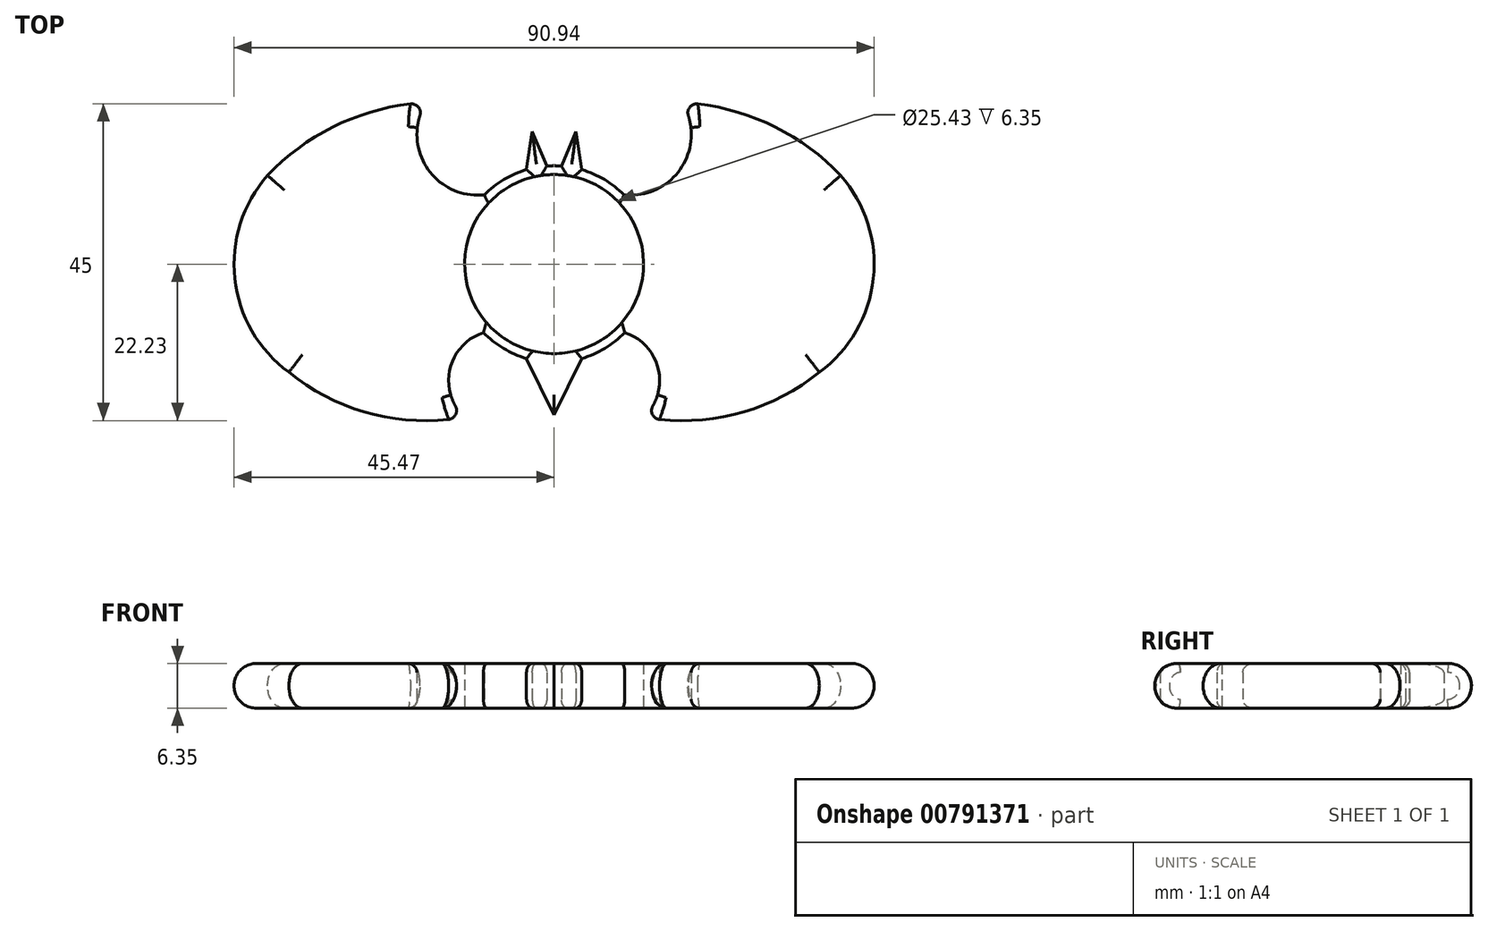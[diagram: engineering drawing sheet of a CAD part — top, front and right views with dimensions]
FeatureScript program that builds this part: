
annotation { "Feature Type Name" : "Feature", "Feature Type Description" : "" }
export const myFeature = defineFeature(function(context is Context, id is Id, definition is map)
    precondition{}
    {
        {
            var Q0;
            Q0=qCreatedBy(makeId("Top.planeOp"),FACE);
            var sketch = newSketch(context, id + "F0", { "sketchPlane" : qUnion([Q0])});
            skCircle(sketch, "E0", {"center": v(0, 0) * mm, "radius": 13.97 * mm});
            skArc(sketch, "E1", {"start": v(37.68, -15.37) * mm, "mid": v(45.36, -2.05) * mm, "end": v(40.7, 12.6) * mm});
            skArc(sketch, "E2", {"start": v(-18.2, 22.95) * mm, "mid": v(-30.45, 19.93) * mm, "end": v(-40.7, 12.6) * mm});
            skArc(sketch, "E3", {"start": v(-18.2, 22.95) * mm, "mid": v(-18.15, 13.81) * mm, "end": v(-9.93, 9.83) * mm});
            skArc(sketch, "E4.trimOffspring", {"start": v(-40.7, 12.6) * mm, "mid": v(-45.36, -2.05) * mm, "end": v(-37.68, -15.37) * mm});
            skArc(sketch, "E5.MirrorCS", {"start": v(18.2, 22.95) * mm, "mid": v(18.15, 13.81) * mm, "end": v(9.93, 9.83) * mm});
            skArc(sketch, "E6.MirrorCS", {"start": v(18.2, 22.95) * mm, "mid": v(30.45, 19.93) * mm, "end": v(40.7, 12.6) * mm});
            skArc(sketch, "E7", {"start": v(-37.68, -15.37) * mm, "mid": v(-25.91, -21.27) * mm, "end": v(-12.76, -21.74) * mm});
            skArc(sketch, "E8", {"start": v(-10.03, -9.72) * mm, "mid": v(-14.81, -14.95) * mm, "end": v(-12.76, -21.74) * mm});
            skArc(sketch, "E9.MirrorCS", {"start": v(10.03, -9.72) * mm, "mid": v(14.81, -14.95) * mm, "end": v(12.76, -21.74) * mm});
            skArc(sketch, "E10.MirrorCS", {"start": v(37.68, -15.37) * mm, "mid": v(25.91, -21.27) * mm, "end": v(12.76, -21.74) * mm});
            skPoint(sketch, "E11.end.orphan", {"position": v(2.34, 18.82) * mm});
            skPoint(sketch, "E12.orphan", {"position": v(3.92, 13.4) * mm});
            skPoint(sketch, "E13.end.orphan", {"position": v(-1.04, 13.93) * mm});
            skPoint(sketch, "E14.end.orphan", {"position": v(-2.23, 18.82) * mm});
            skPoint(sketch, "E15.MirrorCS.end.orphan", {"position": v(1.04, 13.93) * mm});
            skPoint(sketch, "E15.MirrorCS.start.orphan", {"position": v(2.23, 18.82) * mm});
            skPoint(sketch, "E16.end.orphan", {"position": v(-4.8, 18.35) * mm});
            skPoint(sketch, "E17.MirrorCS.end.orphan", {"position": v(4.8, 18.35) * mm});
            skLineSegment(sketch, "E18", {"start": v(-1.04, 13.93) * mm, "end": v(-3.1, 18.83) * mm});
            skLineSegment(sketch, "E19", {"start": v(-3.1, 18.83) * mm, "end": v(-3.92, 13.4) * mm});
            skLineSegment(sketch, "E20.MirrorCS", {"start": v(1.04, 13.93) * mm, "end": v(3.1, 18.83) * mm});
            skLineSegment(sketch, "E21.MirrorCS", {"start": v(3.1, 18.83) * mm, "end": v(3.92, 13.4) * mm});
            skPoint(sketch, "E22.end.orphan", {"position": v(0, -21.45) * mm});
            skPoint(sketch, "E22.start.orphan", {"position": v(-4.01, -13.38) * mm});
            skPoint(sketch, "E23.MirrorCS.start.orphan", {"position": v(4.01, -13.38) * mm});
            skPoint(sketch, "E24.MirrorCS.end.orphan", {"position": v(-3.92, -13.4) * mm});
            skPoint(sketch, "E24.MirrorCS.start.orphan", {"position": v(-3.1, -18.83) * mm});
            skLineSegment(sketch, "E25", {"start": v(-3.92, -13.4) * mm, "end": v(0, -21.45) * mm});
            skLineSegment(sketch, "E26.MirrorCS", {"start": v(3.92, -13.4) * mm, "end": v(0, -21.45) * mm});
            skLineSegment(sketch, "E27", {"start": v(-26.42, 0) * mm, "end": v(-31.16, 0) * mm});
            skLineSegment(sketch, "E28", {"start": v(26.42, 0) * mm, "end": v(31.16, 0) * mm});
            skCircle(sketch, "E29", {"center": v(0, 0) * mm, "radius": 12.71 * mm});
            skSolve(sketch);
        }
        {
            var Q0;
            Q0=qSketchRegion(id+"F0",true);
            extrude(context, id + "F1", {"entities" : qUnion([Q0]), "depth" : 6.35 * mm, "offsetDistance" : 25.4 * mm});
        }
        {
            var Q0;
            Q0=makeQuery(id+"F1.opExtrude","CAP_EDGE",EDGE,{"disambiguationData":[OSD([sQuery(id+"F0.wireOp",EDGE,"E4.trimOffspring")])],"isStart":false});
            var Q1;
            Q1=makeQuery(id+"F1.opExtrude","CAP_EDGE",EDGE,{"disambiguationData":[OSD([sQuery(id+"F0.wireOp",EDGE,"E1")])],"isStart":false});
            var Q2;
            Q2=makeQuery(id+"F1.opExtrude","CAP_EDGE",EDGE,{"disambiguationData":[OSD([sQuery(id+"F0.wireOp",EDGE,"E1")])],"isStart":true});
            var Q3;
            Q3=makeQuery(id+"F1.opExtrude","CAP_EDGE",EDGE,{"disambiguationData":[OSD([sQuery(id+"F0.wireOp",EDGE,"E4.trimOffspring")])],"isStart":true});
            fillet(context, id + "F2", {"entities" : qUnion([Q0, Q1, Q2, Q3]), "radius" : 3.17 * mm, "tangentPropagation" : true, "allowEdgeOverflow" : false});
        }
        {
            var Q0;
            Q0=makeQuery(id+"F2.opFillet","BLEND_EDGE",EDGE,{"blendedFrom":[makeQuery(id+"F1.opExtrude","CAP_EDGE",EDGE,{"disambiguationData":[OSD([sQuery(id+"F0.wireOp",EDGE,"E4.trimOffspring")])],"isStart":false}),makeQuery(id+"F1.opExtrude","SWEPT_FACE",FACE,{"disambiguationData":[OSD([sQuery(id+"F0.wireOp",EDGE,"E3")])]})],"blendedInto":[makeQuery(id+"F1.opExtrude","SWEPT_FACE",FACE,{"disambiguationData":[OSD([sQuery(id+"F0.wireOp",EDGE,"E3")])]})]});
            var Q1;
            Q1=makeQuery(id+"F2.opFillet","BLEND_EDGE",EDGE,{"blendedFrom":[makeQuery(id+"F1.opExtrude","CAP_EDGE",EDGE,{"disambiguationData":[OSD([sQuery(id+"F0.wireOp",EDGE,"E4.trimOffspring")])],"isStart":true}),makeQuery(id+"F1.opExtrude","SWEPT_FACE",FACE,{"disambiguationData":[OSD([sQuery(id+"F0.wireOp",EDGE,"E3")])]})],"blendedInto":[makeQuery(id+"F1.opExtrude","SWEPT_FACE",FACE,{"disambiguationData":[OSD([sQuery(id+"F0.wireOp",EDGE,"E3")])]})]});
            var Q2;
            Q2=makeQuery(id+"F1.opExtrude","CAP_EDGE",EDGE,{"disambiguationData":[OSD([sQuery(id+"F0.wireOp",EDGE,"E8")])],"isStart":false});
            var Q3;
            Q3=makeQuery(id+"F1.opExtrude","CAP_EDGE",EDGE,{"disambiguationData":[OSD([sQuery(id+"F0.wireOp",EDGE,"E9.MirrorCS")])],"isStart":false});
            var Q4;
            Q4=makeQuery(id+"F1.opExtrude","CAP_EDGE",EDGE,{"disambiguationData":[OSD([sQuery(id+"F0.wireOp",EDGE,"E5.MirrorCS")])],"isStart":false});
            var Q5;
            {var subQ0=sQuery(id+"F0.wireOp",EDGE,"E0");Q5=makeQuery(id+"F1.opExtrude","CAP_EDGE",EDGE,{"disambiguationData":[OSD([subQ0]),TDD([makeQuery(id+"F0.imprint","IMPRINT",EDGE,{"disambiguationData":[TD([[makeQuery(id+"F0.imprint","INTERSECT",VERTEX,{"derivedFrom":[subQ0,sQuery(id+"F0.wireOp",EDGE,"E3")]}),1.0]])],"derivedFrom":subQ0})])],"isStart":false});}
            var Q6;
            Q6=makeQuery(id+"F1.opExtrude","CAP_EDGE",EDGE,{"disambiguationData":[OSD([sQuery(id+"F0.wireOp",EDGE,"E19")])],"isStart":false});
            var Q7;
            {var subQ0=sQuery(id+"F0.wireOp",EDGE,"E0");Q7=makeQuery(id+"F1.opExtrude","CAP_EDGE",EDGE,{"disambiguationData":[OSD([subQ0]),TDD([makeQuery(id+"F0.imprint","IMPRINT",EDGE,{"disambiguationData":[TD([[makeQuery(id+"F0.imprint","INTERSECT",VERTEX,{"derivedFrom":[subQ0,sQuery(id+"F0.wireOp",EDGE,"E18")]}),1.0]])],"derivedFrom":subQ0})])],"isStart":false});}
            var Q8;
            Q8=makeQuery(id+"F1.opExtrude","CAP_EDGE",EDGE,{"disambiguationData":[OSD([sQuery(id+"F0.wireOp",EDGE,"E20.MirrorCS")])],"isStart":false});
            var Q9;
            {var subQ0=sQuery(id+"F0.wireOp",EDGE,"E0");Q9=makeQuery(id+"F1.opExtrude","CAP_EDGE",EDGE,{"disambiguationData":[OSD([subQ0]),TDD([makeQuery(id+"F0.imprint","IMPRINT",EDGE,{"disambiguationData":[TD([[makeQuery(id+"F0.imprint","INTERSECT",VERTEX,{"derivedFrom":[subQ0,sQuery(id+"F0.wireOp",EDGE,"E5.MirrorCS")]}),-1.0]])],"derivedFrom":subQ0})])],"isStart":false});}
            var Q10;
            {var subQ0=sQuery(id+"F0.wireOp",EDGE,"E0");Q10=makeQuery(id+"F1.opExtrude","CAP_EDGE",EDGE,{"disambiguationData":[OSD([subQ0]),TDD([makeQuery(id+"F0.imprint","IMPRINT",EDGE,{"disambiguationData":[TD([[makeQuery(id+"F0.imprint","INTERSECT",VERTEX,{"derivedFrom":[subQ0,sQuery(id+"F0.wireOp",EDGE,"E5.MirrorCS")]}),-1.0]])],"derivedFrom":subQ0})])],"isStart":true});}
            var Q11;
            Q11=makeQuery(id+"F1.opExtrude","CAP_EDGE",EDGE,{"disambiguationData":[OSD([sQuery(id+"F0.wireOp",EDGE,"E21.MirrorCS")])],"isStart":true});
            var Q12;
            {var subQ0=sQuery(id+"F0.wireOp",EDGE,"E0");Q12=makeQuery(id+"F1.opExtrude","CAP_EDGE",EDGE,{"disambiguationData":[OSD([subQ0]),TDD([makeQuery(id+"F0.imprint","IMPRINT",EDGE,{"disambiguationData":[TD([[makeQuery(id+"F0.imprint","INTERSECT",VERTEX,{"derivedFrom":[subQ0,sQuery(id+"F0.wireOp",EDGE,"E18")]}),1.0]])],"derivedFrom":subQ0})])],"isStart":true});}
            var Q13;
            Q13=makeQuery(id+"F1.opExtrude","CAP_EDGE",EDGE,{"disambiguationData":[OSD([sQuery(id+"F0.wireOp",EDGE,"E18")])],"isStart":true});
            var Q14;
            Q14=makeQuery(id+"F1.opExtrude","CAP_EDGE",EDGE,{"disambiguationData":[OSD([sQuery(id+"F0.wireOp",EDGE,"E19")])],"isStart":true});
            var Q15;
            {var subQ0=sQuery(id+"F0.wireOp",EDGE,"E0");Q15=makeQuery(id+"F1.opExtrude","CAP_EDGE",EDGE,{"disambiguationData":[OSD([subQ0]),TDD([makeQuery(id+"F0.imprint","IMPRINT",EDGE,{"disambiguationData":[TD([[makeQuery(id+"F0.imprint","INTERSECT",VERTEX,{"derivedFrom":[subQ0,sQuery(id+"F0.wireOp",EDGE,"E3")]}),1.0]])],"derivedFrom":subQ0})])],"isStart":true});}
            var Q16;
            {var subQ0=sQuery(id+"F0.wireOp",EDGE,"E0");Q16=makeQuery(id+"F1.opExtrude","CAP_EDGE",EDGE,{"disambiguationData":[OSD([subQ0]),TDD([makeQuery(id+"F0.imprint","IMPRINT",EDGE,{"disambiguationData":[TD([[makeQuery(id+"F0.imprint","INTERSECT",VERTEX,{"derivedFrom":[subQ0,sQuery(id+"F0.wireOp",EDGE,"E8")]}),-1.0]])],"derivedFrom":subQ0})])],"isStart":false});}
            var Q17;
            Q17=makeQuery(id+"F1.opExtrude","CAP_EDGE",EDGE,{"disambiguationData":[OSD([sQuery(id+"F0.wireOp",EDGE,"E25")])],"isStart":false});
            var Q18;
            Q18=makeQuery(id+"F1.opExtrude","CAP_EDGE",EDGE,{"disambiguationData":[OSD([sQuery(id+"F0.wireOp",EDGE,"E26.MirrorCS")])],"isStart":false});
            var Q19;
            {var subQ0=sQuery(id+"F0.wireOp",EDGE,"E0");Q19=makeQuery(id+"F1.opExtrude","CAP_EDGE",EDGE,{"disambiguationData":[OSD([subQ0]),TDD([makeQuery(id+"F0.imprint","IMPRINT",EDGE,{"disambiguationData":[TD([[makeQuery(id+"F0.imprint","INTERSECT",VERTEX,{"derivedFrom":[subQ0,sQuery(id+"F0.wireOp",EDGE,"E9.MirrorCS")]}),1.0]])],"derivedFrom":subQ0})])],"isStart":false});}
            var Q20;
            {var subQ0=sQuery(id+"F0.wireOp",EDGE,"E0");Q20=makeQuery(id+"F1.opExtrude","CAP_EDGE",EDGE,{"disambiguationData":[OSD([subQ0]),TDD([makeQuery(id+"F0.imprint","IMPRINT",EDGE,{"disambiguationData":[TD([[makeQuery(id+"F0.imprint","INTERSECT",VERTEX,{"derivedFrom":[subQ0,sQuery(id+"F0.wireOp",EDGE,"E9.MirrorCS")]}),1.0]])],"derivedFrom":subQ0})])],"isStart":true});}
            var Q21;
            Q21=makeQuery(id+"F1.opExtrude","CAP_EDGE",EDGE,{"disambiguationData":[OSD([sQuery(id+"F0.wireOp",EDGE,"E26.MirrorCS")])],"isStart":true});
            var Q22;
            Q22=makeQuery(id+"F1.opExtrude","CAP_EDGE",EDGE,{"disambiguationData":[OSD([sQuery(id+"F0.wireOp",EDGE,"E25")])],"isStart":true});
            var Q23;
            {var subQ0=sQuery(id+"F0.wireOp",EDGE,"E0");Q23=makeQuery(id+"F1.opExtrude","CAP_EDGE",EDGE,{"disambiguationData":[OSD([subQ0]),TDD([makeQuery(id+"F0.imprint","IMPRINT",EDGE,{"disambiguationData":[TD([[makeQuery(id+"F0.imprint","INTERSECT",VERTEX,{"derivedFrom":[subQ0,sQuery(id+"F0.wireOp",EDGE,"E8")]}),-1.0]])],"derivedFrom":subQ0})])],"isStart":true});}
            var Q24;
            Q24=makeQuery(id+"F1.opExtrude","CAP_EDGE",EDGE,{"disambiguationData":[OSD([sQuery(id+"F0.wireOp",EDGE,"E20.MirrorCS")])],"isStart":true});
            var Q25;
            Q25=makeQuery(id+"F1.opExtrude","CAP_EDGE",EDGE,{"disambiguationData":[OSD([sQuery(id+"F0.wireOp",EDGE,"E21.MirrorCS")])],"isStart":false});
            var Q26;
            Q26=makeQuery(id+"F1.opExtrude","CAP_EDGE",EDGE,{"disambiguationData":[OSD([sQuery(id+"F0.wireOp",EDGE,"E18")])],"isStart":false});
            fillet(context, id + "F3", {"entities" : qUnion([Q0, Q1, Q2, Q3, Q4, Q5, Q6, Q7, Q8, Q9, Q10, Q11, Q12, Q13, Q14, Q15, Q16, Q17, Q18, Q19, Q20, Q21, Q22, Q23, Q24, Q25, Q26]), "radius" : 1.27 * mm, "tangentPropagation" : true, "allowEdgeOverflow" : false});
        }
    });
